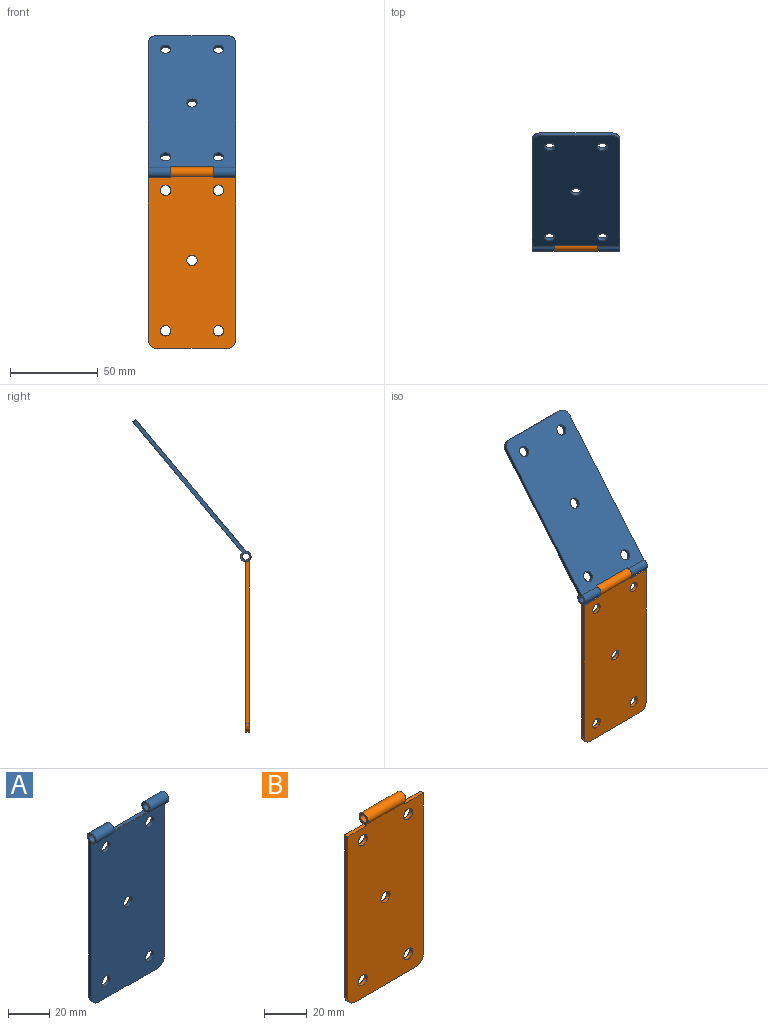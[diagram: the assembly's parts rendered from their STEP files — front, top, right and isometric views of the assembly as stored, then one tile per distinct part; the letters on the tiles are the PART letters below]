
ASSEMBLY  parts=2 mates=1
PART A: 18 faces, bbox 50x6x103 mm
  f0: plane 97.76x50mm, normal (0,1,0), area 4718.9mm2, adj f3,f4,f5,f6,f7,f8,f10,f11
  f1: plane 97x50mm, normal (0,-1,0), area 4697.9mm2, adj f3,f4,f5,f6,f7,f8,f13,f14
  f2: cylinder r=2mm len=12.5mm, axis (-1,0,0), area 157.1mm2, adj f4,f10
  f3: cylinder r=3mm len=50mm, axis (-1,0,0), area 433.3mm2, adj f0,f1,f4,f5,f10,f11,f12
  f4: plane 98x6mm, normal (1,0,0), area 200.2mm2, adj f0,f1,f2,f3,f8
  f5: plane 98x6mm, normal (-1,0,0), area 200.2mm2, adj f0,f1,f3,f7,f9
  f6: plane 40x2mm, normal (0,0,-1), area 80mm2, adj f0,f1,f7,f8
  f7: cylinder r=5mm len=5mm, axis (0,1,0), area 15.7mm2, adj f0,f1,f5,f6
  f8: cylinder r=5mm len=5mm, axis (0,-1,0), area 15.7mm2, adj f0,f1,f4,f6
  f9: cylinder r=2mm len=12.5mm, axis (-1,0,0), area 157.1mm2, adj f5,f11
  f10: plane 6x5.93mm, normal (-1,0,0), area 16mm2, adj f0,f2,f3,f12
  f11: plane 6x5.93mm, normal (1,0,0), area 16mm2, adj f0,f3,f9,f12
  f12: plane 25x2.66mm, normal (0,0,1), area 66.6mm2, adj f0,f3,f10,f11
  f13: cylinder r=3mm len=6mm, axis (0,-1,0), area 37.7mm2, adj f0,f1
  f14: cylinder r=3mm len=6mm, axis (0,-1,0), area 37.7mm2, adj f0,f1
  f15: cylinder r=3mm len=6mm, axis (0,-1,0), area 37.7mm2, adj f0,f1
  f16: cylinder r=3mm len=6mm, axis (0,-1,0), area 37.7mm2, adj f0,f1
  f17: cylinder r=3mm len=6mm, axis (0,-1,0), area 37.7mm2, adj f0,f1
PART B: 18 faces, bbox 50x6x103 mm
  f0: plane 97.76x50mm, normal (0,-1,0), area 4717mm2, adj f1,f2,f4,f5,f6,f7,f8,f9
  f1: plane 92x2mm, normal (1,0,0), area 184mm2, adj f0,f3,f7,f13
  f2: cylinder r=3mm len=25mm, axis (-1,0,0), area 416.5mm2, adj f0,f3,f14,f16
  f3: plane 97x50mm, normal (0,1,0), area 4697.9mm2, adj f1,f2,f4,f5,f6,f7,f8,f9
  f4: plane 92x2mm, normal (-1,0,0), area 184mm2, adj f0,f3,f6,f15
  f5: plane 40x2mm, normal (0,0,-1), area 80mm2, adj f0,f3,f6,f7
  f6: cylinder r=5mm len=5mm, axis (0,1,0), area 15.7mm2, adj f0,f3,f4,f5
  f7: cylinder r=5mm len=5mm, axis (0,-1,0), area 15.7mm2, adj f0,f1,f3,f5
  f8: cylinder r=3mm len=6mm, axis (0,-1,0), area 37.7mm2, adj f0,f3
  f9: cylinder r=3mm len=6mm, axis (0,-1,0), area 37.7mm2, adj f0,f3
  f10: cylinder r=3mm len=6mm, axis (0,-1,0), area 37.7mm2, adj f0,f3
  f11: cylinder r=3mm len=6mm, axis (0,-1,0), area 37.7mm2, adj f0,f3
  f12: cylinder r=3mm len=6mm, axis (0,-1,0), area 37.7mm2, adj f0,f3
  f13: plane 12.5x2mm, normal (0,0,1), area 25mm2, adj f0,f1,f3,f14
  f14: plane 6x6mm, normal (1,0,0), area 16.2mm2, adj f0,f2,f13,f17
  f15: plane 12.5x2mm, normal (0,0,1), area 25mm2, adj f0,f3,f4,f16
  f16: plane 6x6mm, normal (-1,0,0), area 16.2mm2, adj f0,f2,f15,f17
  f17: cylinder r=2mm len=25mm, axis (-1,0,0), area 314.2mm2, adj f14,f16
PLACE A rot(axis=(1,0,0),140.1deg) t=(-25,31.34,88.97)mm
PLACE B t=(-25,-1,0)mm
MATE revolute B.f2 <-> A.f2  axis (-1,0,0) through (-12.5,0,50)mm
